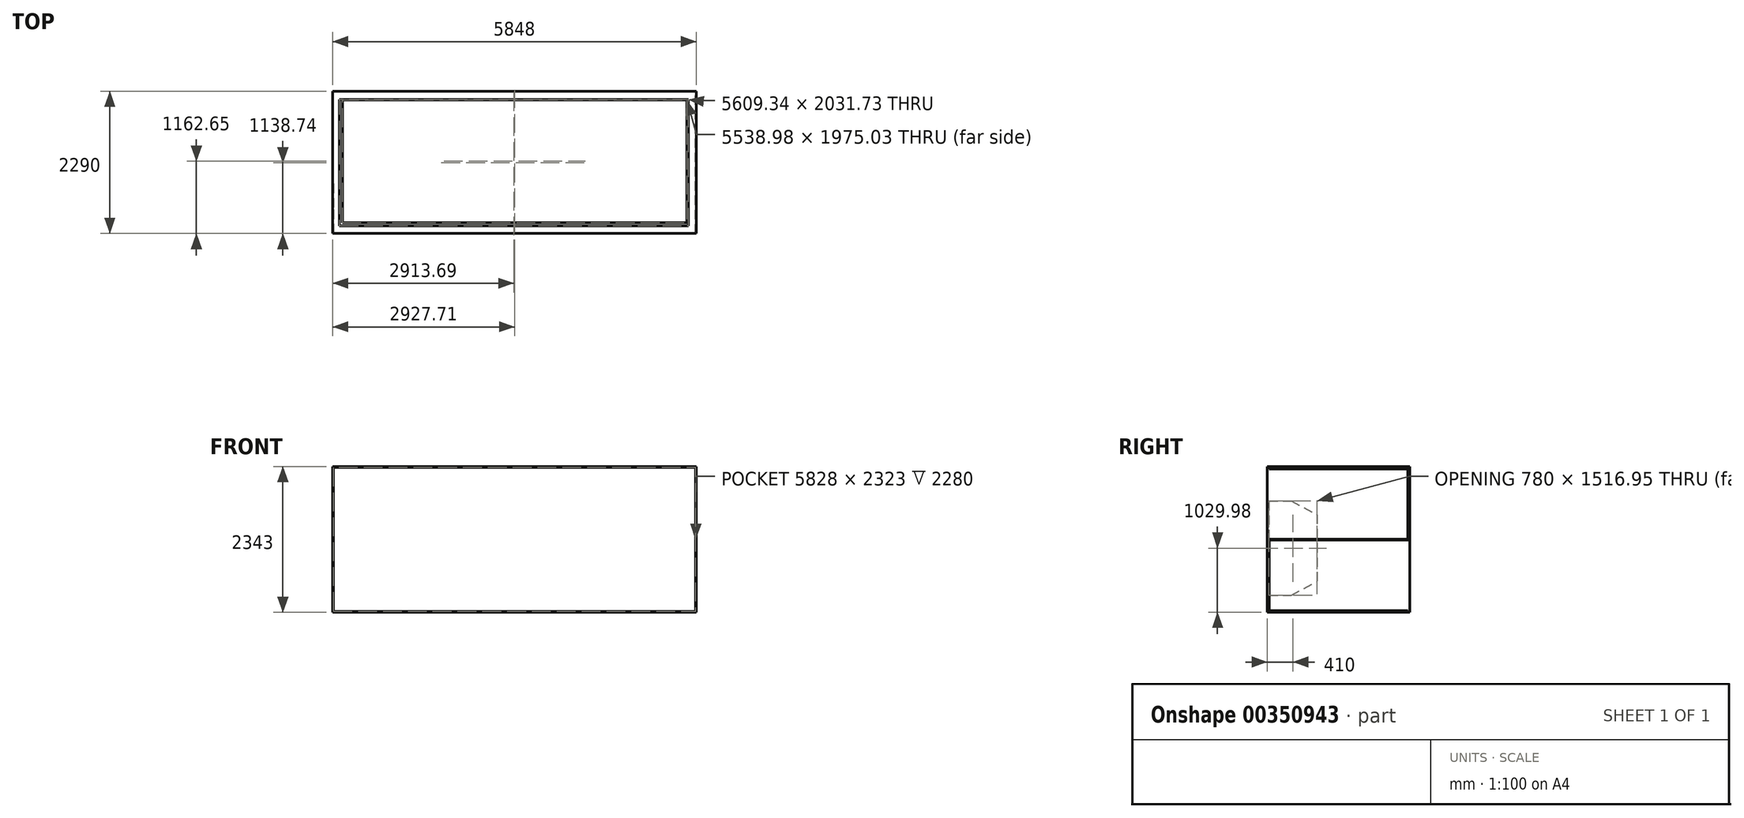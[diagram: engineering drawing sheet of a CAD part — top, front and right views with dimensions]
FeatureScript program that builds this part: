
annotation { "Feature Type Name" : "Feature", "Feature Type Description" : "" }
export const myFeature = defineFeature(function(context is Context, id is Id, definition is map)
    precondition{}
    {
        {
            var Q0;
            Q0=qCreatedBy(makeId("Front.planeOp"),FACE);
            var sketch = newSketch(context, id + "F0", { "sketchPlane" : qUnion([Q0])});
            skLineSegment(sketch, "E0.bottom", {"start": v(-2924, 1171.5) * mm, "end": v(2924, 1171.5) * mm});
            skLineSegment(sketch, "E0.top", {"start": v(-2924, -1171.5) * mm, "end": v(2924, -1171.5) * mm});
            skLineSegment(sketch, "E0.left", {"start": v(-2924, 1171.5) * mm, "end": v(-2924, -1171.5) * mm});
            skLineSegment(sketch, "E0.right", {"start": v(2924, 1171.5) * mm, "end": v(2924, -1171.5) * mm});
            skPoint(sketch, "E0.middle", {"position": v(0, 0) * mm});
            skLineSegment(sketch, "E1.bottom", {"start": v(-2914, 1161.5) * mm, "end": v(2914, 1161.5) * mm});
            skLineSegment(sketch, "E1.top", {"start": v(-2914, -1161.5) * mm, "end": v(2914, -1161.5) * mm});
            skLineSegment(sketch, "E1.left", {"start": v(-2914, 1161.5) * mm, "end": v(-2914, -1161.5) * mm});
            skLineSegment(sketch, "E1.right", {"start": v(2914, 1161.5) * mm, "end": v(2914, -1161.5) * mm});
            skSolve(sketch);
        }
        {
            var Q0;
            Q0 = qSketchRegion(id + "F0", true);
            extrude(context, id + "F1", {"entities" : qUnion([Q0]), "depth" : 2280 * mm});
        }
        {
            var Q0;
            Q0=makeQuery(id+"F1.opExtrude","CAP_FACE",FACE,{"disambiguationData":[OSD([sQuery(id+"F0.wireOp",EDGE,"E0.bottom"),sQuery(id+"F0.wireOp",EDGE,"E0.top"),sQuery(id+"F0.wireOp",EDGE,"E0.left"),sQuery(id+"F0.wireOp",EDGE,"E0.right"),sQuery(id+"F0.wireOp",EDGE,"E1.bottom"),sQuery(id+"F0.wireOp",EDGE,"E1.top"),sQuery(id+"F0.wireOp",EDGE,"E1.left"),sQuery(id+"F0.wireOp",EDGE,"E1.right")])],"isStart":true});
            var sketch = newSketch(context, id + "F2", { "sketchPlane" : qUnion([Q0])});
            skLineSegment(sketch, "E2.bottom", {"start": v(-2924, 1171.5) * mm, "end": v(2924, 1171.5) * mm});
            skLineSegment(sketch, "E2.top", {"start": v(-2924, -1171.5) * mm, "end": v(2924, -1171.5) * mm});
            skLineSegment(sketch, "E2.left", {"start": v(-2924, 1171.5) * mm, "end": v(-2924, -1171.5) * mm});
            skLineSegment(sketch, "E2.right", {"start": v(2924, 1171.5) * mm, "end": v(2924, -1171.5) * mm});
            skSolve(sketch);
        }
        {
            var Q0;
            Q0=makeQuery(id+"F2.imprint","IMPRINT",FACE,{"disambiguationData":[TD([[makeQuery(id+"F2.imprint","IMPRINT",EDGE,{"derivedFrom":sQuery(id+"F2.wireOp",EDGE,"E2.bottom")}),1.0]])]});
            var Q1;
            Q1=makeQuery(id+"F2.imprint","IMPRINT",FACE,{"disambiguationData":[TD([[makeQuery(id+"F2.imprint","IMPRINT",EDGE,{"derivedFrom":makeQuery(id+"F1.opExtrude","CAP_EDGE",EDGE,{"disambiguationData":[OSD([sQuery(id+"F0.wireOp",EDGE,"E1.bottom")])],"isStart":true})}),1.0]])]});
            extrude(context, id + "F3", {"entities" : qUnion([Q0, Q1]), "operationType" : NewBodyOperationType.ADD, "depth" : 10 * mm});
        }
        {
            var Q0;
            Q0=makeQuery(id+"F3.boolean.opBoolean","MERGE",FACE,{"derivedFrom":[makeQuery(id+"F1.opExtrude","SWEPT_FACE",FACE,{"disambiguationData":[OSD([sQuery(id+"F0.wireOp",EDGE,"E0.top")])]}),makeQuery(id+"F3.opExtrude","SWEPT_FACE",FACE,{"disambiguationData":[OSD([sQuery(id+"F2.wireOp",EDGE,"E2.top")])]})]});
            var sketch = newSketch(context, id + "F4", { "sketchPlane" : qUnion([Q0])});
            skLineSegment(sketch, "E3.bottom", {"start": v(-2765.78, 2104.86) * mm, "end": v(2773.2, 2104.86) * mm});
            skLineSegment(sketch, "E3.top", {"start": v(-2765.78, 129.84) * mm, "end": v(2773.2, 129.84) * mm});
            skLineSegment(sketch, "E3.left", {"start": v(-2765.78, 2104.86) * mm, "end": v(-2765.78, 129.84) * mm});
            skLineSegment(sketch, "E3.right", {"start": v(2773.2, 2104.86) * mm, "end": v(2773.2, 129.84) * mm});
            skSolve(sketch);
        }
        {
            var Q0;
            Q0 = qSketchRegion(id + "F4", true);
            extrude(context, id + "F5", {"entities" : qUnion([Q0]), "operationType" : NewBodyOperationType.REMOVE, "oppositeDirection" : true, "depth" : 25 * mm});
        }
        {
            var Q0;
            Q0=makeQuery(id+"F3.boolean.opBoolean","MERGE",FACE,{"derivedFrom":[makeQuery(id+"F1.opExtrude","SWEPT_FACE",FACE,{"disambiguationData":[OSD([sQuery(id+"F0.wireOp",EDGE,"E0.left")])]}),makeQuery(id+"F3.opExtrude","SWEPT_FACE",FACE,{"disambiguationData":[OSD([sQuery(id+"F2.wireOp",EDGE,"E2.right")])]})]});
            var sketch = newSketch(context, id + "F6", { "sketchPlane" : qUnion([Q0])});
            skLineSegment(sketch, "E4.bottom", {"start": v(2280, 900) * mm, "end": v(1480, 900) * mm});
            skLineSegment(sketch, "E4.top", {"start": v(2280, -900) * mm, "end": v(1480, -900) * mm});
            skLineSegment(sketch, "E4.left", {"start": v(2280, 900) * mm, "end": v(2280, -900) * mm});
            skLineSegment(sketch, "E4.right", {"start": v(1480, 900) * mm, "end": v(1480, -900) * mm});
            skLineSegment(sketch, "E5", {"start": v(2053.32, -900) * mm, "end": v(2053.32, -1171.5) * mm});
            skLineSegment(sketch, "E6", {"start": v(1880, 900) * mm, "end": v(1880, 1171.5) * mm});
            skLineSegment(sketch, "E7", {"start": v(2260, 900) * mm, "end": v(2260, -900) * mm});
            skLineSegment(sketch, "E8", {"start": v(2260, 616.95) * mm, "end": v(1480, 616.95) * mm});
            skLineSegment(sketch, "E9", {"start": v(1898.04, -900) * mm, "end": v(1480, -680.96) * mm});
            skLineSegment(sketch, "E10", {"start": v(1898.04, 616.95) * mm, "end": v(1480, 397.91) * mm});
            skPoint(sketch, "E11", {"position": v(1870, 616.95) * mm});
            skSolve(sketch);
        }
        {
            var Q0;
            {var subQ6=sQuery(id+"F6.wireOp",EDGE,"4RWK2Urh-KRNU-SJh8-0ovm-i2RlFRTBqIvG");Q0=makeQuery(id+"F6.imprint","IMPRINT",FACE,{"disambiguationData":[TD([[makeQuery(id+"F6.imprint","IMPRINT",EDGE,{"derivedFrom":subQ6}),1.0]])]});}
            var Q1;
            {var subQ6=sQuery(id+"F6.wireOp",EDGE,"E9");Q1=makeQuery(id+"F6.imprint","IMPRINT",FACE,{"disambiguationData":[TD([[makeQuery(id+"F6.imprint","IMPRINT",EDGE,{"derivedFrom":subQ6}),-1.0]])]});}
            extrude(context, id + "F7", {"entities" : qUnion([Q0, Q1]), "operationType" : NewBodyOperationType.REMOVE, "oppositeDirection" : true, "depth" : 25 * mm});
        }
        {
            var Q0;
            Q0=makeQuery(id+"F3.boolean.opBoolean","MERGE",FACE,{"derivedFrom":[makeQuery(id+"F1.opExtrude","SWEPT_FACE",FACE,{"disambiguationData":[OSD([sQuery(id+"F0.wireOp",EDGE,"E0.right")])]}),makeQuery(id+"F3.opExtrude","SWEPT_FACE",FACE,{"disambiguationData":[OSD([sQuery(id+"F2.wireOp",EDGE,"E2.left")])]})]});
            var sketch = newSketch(context, id + "F8", { "sketchPlane" : qUnion([Q0])});
            skLineSegment(sketch, "E12", {"start": v(-2280, 1.7) * mm, "end": v(10, 1.7) * mm});
            skLineSegment(sketch, "E13", {"start": v(-2280, -8.3) * mm, "end": v(10, -8.3) * mm});
            skLineSegment(sketch, "E14", {"start": v(-10, -8.3) * mm, "end": v(-10, 1.7) * mm});
            skLineSegment(sketch, "E15", {"start": v(-2260, 1.7) * mm, "end": v(-2260, -8.3) * mm});
            skLineSegment(sketch, "E16.bottom", {"start": v(-2260, -8.3) * mm, "end": v(-2248.7, -8.3) * mm});
            skLineSegment(sketch, "E17.bottom", {"start": v(-10, -8.3) * mm, "end": v(-20, -8.3) * mm});
            skLineSegment(sketch, "E17.top", {"start": v(-10, -1153.3) * mm, "end": v(-20, -1153.3) * mm});
            skLineSegment(sketch, "E17.left", {"start": v(-10, -8.3) * mm, "end": v(-10, -1153.3) * mm});
            skLineSegment(sketch, "E17.right", {"start": v(-20, -8.3) * mm, "end": v(-20, -1153.3) * mm});
            skLineSegment(sketch, "E18.bottom", {"start": v(-20, -1153.3) * mm, "end": v(-2250, -1153.3) * mm});
            skLineSegment(sketch, "E18.top", {"start": v(-20, -1143.3) * mm, "end": v(-2250, -1143.3) * mm});
            skLineSegment(sketch, "E18.left", {"start": v(-20, -1153.3) * mm, "end": v(-20, -1143.3) * mm});
            skLineSegment(sketch, "E18.right", {"start": v(-2250, -1153.3) * mm, "end": v(-2250, -1143.3) * mm});
            skLineSegment(sketch, "E19.bottom", {"start": v(-2250, -1153.3) * mm, "end": v(-2260, -1153.3) * mm});
            skLineSegment(sketch, "E19.top", {"start": v(-2250, -8.3) * mm, "end": v(-2260, -8.3) * mm});
            skLineSegment(sketch, "E19.left", {"start": v(-2250, -1153.3) * mm, "end": v(-2250, -8.3) * mm});
            skLineSegment(sketch, "E19.right", {"start": v(-2260, -1153.3) * mm, "end": v(-2260, -8.3) * mm});
            skLineSegment(sketch, "E20.bottom", {"start": v(-2260, 1.7) * mm, "end": v(-2248.7, 1.7) * mm});
            skLineSegment(sketch, "E20.top", {"start": v(-2260, 1146.7) * mm, "end": v(-2248.7, 1146.7) * mm});
            skLineSegment(sketch, "E20.left", {"start": v(-2260, 1.7) * mm, "end": v(-2260, 1146.7) * mm});
            skLineSegment(sketch, "E20.right", {"start": v(-2248.7, 1.7) * mm, "end": v(-2248.7, 1146.7) * mm});
            skLineSegment(sketch, "E21.bottom", {"start": v(-2248.7, 1146.7) * mm, "end": v(-20, 1146.7) * mm});
            skLineSegment(sketch, "E21.top", {"start": v(-2248.7, 1136.7) * mm, "end": v(-20, 1136.7) * mm});
            skLineSegment(sketch, "E21.left", {"start": v(-2248.7, 1146.7) * mm, "end": v(-2248.7, 1136.7) * mm});
            skLineSegment(sketch, "E21.right", {"start": v(-20, 1146.7) * mm, "end": v(-20, 1136.7) * mm});
            skLineSegment(sketch, "E22.bottom", {"start": v(-20, 1146.7) * mm, "end": v(-10, 1146.7) * mm});
            skLineSegment(sketch, "E22.top", {"start": v(-20, 1.7) * mm, "end": v(-10, 1.7) * mm});
            skLineSegment(sketch, "E22.left", {"start": v(-20, 1146.7) * mm, "end": v(-20, 1.7) * mm});
            skLineSegment(sketch, "E22.right", {"start": v(-10, 1146.7) * mm, "end": v(-10, 1.7) * mm});
            skSolve(sketch);
        }
        {
            var Q0;
            {var subQ0=sQuery(id+"F8.wireOp",EDGE,"E14");Q0=makeQuery(id+"F8.imprint","IMPRINT",FACE,{"disambiguationData":[TD([[makeQuery(id+"F8.imprint","IMPRINT",EDGE,{"derivedFrom":subQ0}),1.0]])]});}
            var Q1;
            {var subQ3=sQuery(id+"F8.wireOp",EDGE,"E22.bottom");Q1=makeQuery(id+"F8.imprint","IMPRINT",FACE,{"disambiguationData":[TD([[makeQuery(id+"F8.imprint","IMPRINT",EDGE,{"derivedFrom":subQ3}),-1.0]])]});}
            var Q2;
            {var subQ0=sQuery(id+"F8.wireOp",EDGE,"E21.bottom");Q2=makeQuery(id+"F8.imprint","IMPRINT",FACE,{"disambiguationData":[TD([[makeQuery(id+"F8.imprint","IMPRINT",EDGE,{"derivedFrom":subQ0}),-1.0]])]});}
            var Q3;
            Q3=makeQuery(id+"F8.imprint","IMPRINT",FACE,{"disambiguationData":[TD([[makeQuery(id+"F8.imprint","IMPRINT",EDGE,{"derivedFrom":sQuery(id+"F8.wireOp",EDGE,"E20.bottom")}),1.0]])]});
            var Q4;
            {var subQ3=sQuery(id+"F8.wireOp",EDGE,"E19.bottom");Q4=makeQuery(id+"F8.imprint","IMPRINT",FACE,{"disambiguationData":[TD([[makeQuery(id+"F8.imprint","IMPRINT",EDGE,{"derivedFrom":subQ3}),-1.0]])]});}
            var Q5;
            {var subQ0=sQuery(id+"F8.wireOp",EDGE,"E18.bottom");Q5=makeQuery(id+"F8.imprint","IMPRINT",FACE,{"disambiguationData":[TD([[makeQuery(id+"F8.imprint","IMPRINT",EDGE,{"derivedFrom":subQ0}),-1.0]])]});}
            var Q6;
            Q6=makeQuery(id+"F8.imprint","IMPRINT",FACE,{"disambiguationData":[TD([[makeQuery(id+"F8.imprint","IMPRINT",EDGE,{"derivedFrom":sQuery(id+"F8.wireOp",EDGE,"E17.bottom")}),1.0]])]});
            extrude(context, id + "F9", {"entities" : qUnion([Q0, Q1, Q2, Q3, Q4, Q5, Q6]), "operationType" : NewBodyOperationType.REMOVE, "oppositeDirection" : true, "depth" : 5 * mm});
        }
        {
            var Q0;
            Q0=makeQuery(id+"F3.boolean.opBoolean","MERGE",FACE,{"derivedFrom":[makeQuery(id+"F1.opExtrude","SWEPT_FACE",FACE,{"disambiguationData":[OSD([sQuery(id+"F0.wireOp",EDGE,"E0.bottom")])]}),makeQuery(id+"F3.opExtrude","SWEPT_FACE",FACE,{"disambiguationData":[OSD([sQuery(id+"F2.wireOp",EDGE,"E2.bottom")])]})]});
            var sketch = newSketch(context, id + "F10", { "sketchPlane" : qUnion([Q0])});
            skLineSegment(sketch, "E23.bottom", {"start": v(-2814.98, -125.4) * mm, "end": v(2794.36, -125.4) * mm});
            skLineSegment(sketch, "E23.top", {"start": v(-2814.98, -2157.12) * mm, "end": v(2794.36, -2157.12) * mm});
            skLineSegment(sketch, "E23.left", {"start": v(-2814.98, -125.4) * mm, "end": v(-2814.98, -2157.12) * mm});
            skLineSegment(sketch, "E23.right", {"start": v(2794.36, -125.4) * mm, "end": v(2794.36, -2157.12) * mm});
            skSolve(sketch);
        }
        {
            var Q0;
            Q0 = qSketchRegion(id + "F10", true);
            extrude(context, id + "F11", {"entities" : qUnion([Q0]), "operationType" : NewBodyOperationType.REMOVE, "oppositeDirection" : true, "depth" : 25 * mm});
        }
    });
